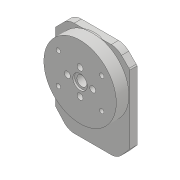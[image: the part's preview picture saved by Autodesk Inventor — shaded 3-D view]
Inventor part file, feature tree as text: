
AUTODESK INVENTOR PART (.ipt)
format: ipt  version: 2018 (Build 220112000, 112)  size: 219,648 bytes
history: native  units: mm
features: sketch x8, extrude x6, other x4, hole x2, pattern_circular x2, fillet x2, projected_geometry x2, plane x1, reference x1
ambient origin geometry x8: Origin, YZ Plane, XZ Plane, XY Plane, X Axis, Y Axis, Z Axis, Center Point
bodies: Solid1 (feature_tree)
feature tree (28):
  extrude  "Extrusion1"  Depth=7.0mm TaperAngle=0.0deg
  extrude  "Extrusion2"  Depth=4.0mm TaperAngle=0.0deg
  hole  "Hole1"  [1 undecoded]
  pattern_circular  "Circular Pattern1"  [2 undecoded]
  extrude  "Extrusion3"  Depth=7.75mm TaperAngle=0.0deg
  extrude  "Extrusion4"  Depth=40.0mm TaperAngle=360.0deg
  extrude  "Extrusion5"  Depth=17.0mm
  pattern_circular  "Circular Pattern2"  [2 undecoded]
  hole  "Hole2"  [1 undecoded]
  fillet  "Fillet1"  Radius=5.0mm
  sketch  "Sketch10"  dims[d21=1.0mm d22=0.0mm d23=5.7mm d24=7.75mm d25=0.0mm d26=40.0mm d27=360.0deg d29=17.0mm d30=24.0mm d31=5.0mm d32=5.0mm d33=2.0mm d34=2.459mm d35=6.0mm d36=9.4mm d37=2.0mm d38=90.0deg d39=8.8mm d40=20.594885mm d43=1.0mm d44=10.0mm d45=0.0mm d46=2.0mm]
  plane  "Work Plane1"
  extrude  "Extrusion7"  Depth=2.0mm
  fillet  "Fillet2"  Radius=1.0mm
  sketch  "Sketch1"  dims[d0=40.0mm d1=7.0mm d2=0.0mm]
  sketch  "Sketch2"  dims[d3=80.4mm d4=4.0mm d5=0.0mm]
  sketch  "Sketch3"  dims[d6=7.0mm]
  sketch  "Sketch4"  dims[d7=3.3mm d8=6.35mm d9=6.3mm d10=2.0mm d11=90.0deg d12=8.0mm d13=20.594885mm d14=40.0mm d15=360.0deg]
  sketch  "Sketch5"  dims[d17=5.5mm]
  sketch  "Sketch6"  dims[d18=10.0mm d19=0.0mm]
  projected_geometry  "Projected Loop1"
  sketch  "Sketch8"  dims[d20=8.0mm]
  projected_geometry  "Projected Loop3"
  reference  "Reference3"
  parser-record x1  (decoder bookkeeping rows leaked as tree rows — omitted from the tree; the rows remain in map.json)
  other  "servocheck.iam"
  other  "bottomarm:1"
  other  "arm1:1"
note: 6 required parameter values undecoded (feature->parameter linkage not recoverable at this tier; creation-order binding heuristic only, values carry confidence <= 0.55)
note: 1 file-system path scrubbed to <path> (originals preserved in map.json)
